FCSTD DOCUMENT  (FreeCAD 0.16R6712 (Git))
Label: LT arm cylinder geometry
License: All rights reserved
LicenseURL: http://en.wikipedia.org/wiki/All_rights_reserved
objects: Sketcher::SketchObject×5
note: 5 computed .brp shape members not serialized (recipe doc carries the construction recipe); baked Part::Feature solids carry a one-line shape summary decoded from their .brp

FEATURE [Sketcher::SketchObject] Sketch  label="16" stroke"
  Placement = pos=(0,0,0) rot=(-1,0,0;4.71239rad)
  sketch-geometry (6):
    g0: LineSegment [constr] StartX=0 StartY=0 StartZ=0 EndX=534.236 EndY=398.933 EndZ=0
    g1: LineSegment [constr] StartX=0 StartY=0 StartZ=0 EndX=0 EndY=557.181 EndZ=0
    g2: LineSegment [constr] StartX=0 StartY=557.181 StartZ=0 EndX=534.236 EndY=398.933 EndZ=0
    g3: LineSegment [constr] StartX=0 StartY=0 StartZ=0 EndX=179.648 EndY=642.092 EndZ=0
    g4: LineSegment [constr] StartX=179.648 StartY=642.092 StartZ=0 EndX=289.148 EndY=1033.46 EndZ=0
    g5: LineSegment [constr] StartX=0 StartY=557.181 StartZ=0 EndX=289.148 EndY=1033.46 EndZ=0
  constraints (16):
    c: Coincident(g0,g-1)
    c: Coincident(g1,g-1)
    c: Vertical(g1)
    c: Coincident(g2,g1)
    c: Coincident(g2,g0)
    c: Coincident(g3,g-1)
    c: Coincident(g4,g3)
    c: Parallel(g4,g3)
    c: Equal(g3,g0)
    c: Coincident(g5,g1)
    c: Coincident(g5,g4)
    c: Equal(g2,g5)
    c: Equal(g2,g1)
    c: Distance(g0) = 666.75
    c: Distance(g4) = 406.4
    c: Angle(g1,g2) = 1.28282
FEATURE [Sketcher::SketchObject] Sketch001  label="24" stroke"
  Placement = pos=(0,0,0) rot=(-1,0,0;4.71239rad)
  sketch-geometry (6):
    g0: LineSegment [constr] StartX=0 StartY=0 StartZ=0 EndX=712.621 EndY=498.983 EndZ=0
    g1: LineSegment [constr] StartX=0 StartY=0 StartZ=0 EndX=0 EndY=758.356 EndZ=0
    g2: LineSegment [constr] StartX=0 StartY=758.356 StartZ=0 EndX=712.621 EndY=498.983 EndZ=0
    g3: LineSegment [constr] StartX=0 StartY=0 StartZ=0 EndX=191.394 EndY=848.635 EndZ=0
    g4: LineSegment [constr] StartX=191.394 StartY=848.635 StartZ=0 EndX=325.509 EndY=1443.3 EndZ=0
    g5: LineSegment [constr] StartX=0 StartY=758.356 StartZ=0 EndX=325.509 EndY=1443.3 EndZ=0
  constraints (16):
    c: Coincident(g0,g-1)
    c: Coincident(g1,g-1)
    c: Vertical(g1)
    c: Coincident(g2,g1)
    c: Coincident(g2,g0)
    c: Coincident(g3,g-1)
    c: Coincident(g4,g3)
    c: Parallel(g4,g3)
    c: Equal(g3,g0)
    c: Coincident(g5,g1)
    c: Coincident(g5,g4)
    c: Equal(g2,g5)
    c: Distance(g0) = 869.95
    c: Equal(g2,g1)
    c: Distance(g4) = 609.6
    c: Angle(g1,g2) = 1.22173
FEATURE [Sketcher::SketchObject] Sketch002  label="30" stroke"
  Placement = pos=(0,0,0) rot=(-1,0,0;4.71239rad)
  sketch-geometry (6):
    g0: LineSegment [constr] StartX=0 StartY=0 StartZ=0 EndX=847.68 EndY=571.522 EndZ=0
    g1: LineSegment [constr] StartX=0 StartY=0 StartZ=0 EndX=0 EndY=914.4 EndZ=0
    g2: LineSegment [constr] StartX=0 StartY=914.4 StartZ=0 EndX=847.68 EndY=571.522 EndZ=0
    g3: LineSegment [constr] StartX=0 StartY=0 StartZ=0 EndX=224.033 EndY=997.501 EndZ=0
    g4: LineSegment [constr] StartX=224.033 StartY=997.501 StartZ=0 EndX=391.014 EndY=1740.98 EndZ=0
    g5: LineSegment [constr] StartX=0 StartY=914.4 StartZ=0 EndX=391.014 EndY=1740.98 EndZ=0
  constraints (16):
    c: Coincident(g0,g-1)
    c: Coincident(g1,g-1)
    c: Vertical(g1)
    c: Coincident(g2,g1)
    c: Coincident(g2,g0)
    c: Coincident(g3,g-1)
    c: Coincident(g4,g3)
    c: Parallel(g4,g3)
    c: Equal(g3,g0)
    c: Coincident(g5,g1)
    c: Coincident(g5,g4)
    c: Equal(g2,g5)
    c: Distance(g0) = 1022.35
    c: Equal(g2,g1)
    c: Distance(g4) = 762
    c: Distance(g1) = 914.4
FEATURE [Sketcher::SketchObject] Sketch003  label="36" stroke"
  Placement = pos=(0,0,0) rot=(-1,0,0;4.71239rad)
  sketch-geometry (6):
    g0: LineSegment [constr] StartX=0 StartY=0 StartZ=0 EndX=985.626 EndY=639.202 EndZ=0
    g1: LineSegment [constr] StartX=0 StartY=0 StartZ=0 EndX=0 EndY=1079.5 EndZ=0
    g2: LineSegment [constr] StartX=0 StartY=1079.5 StartZ=0 EndX=985.626 EndY=639.202 EndZ=0
    g3: LineSegment [constr] StartX=0 StartY=0 StartZ=0 EndX=296.398 EndY=1136.74 EndZ=0
    g4: LineSegment [constr] StartX=296.398 StartY=1136.74 StartZ=0 EndX=527.109 EndY=2021.56 EndZ=0
    g5: LineSegment [constr] StartX=0 StartY=1079.5 StartZ=0 EndX=527.109 EndY=2021.56 EndZ=0
  constraints (16):
    c: Coincident(g0,g-1)
    c: Coincident(g1,g-1)
    c: Vertical(g1)
    c: Coincident(g2,g1)
    c: Coincident(g2,g0)
    c: Coincident(g3,g-1)
    c: Coincident(g4,g3)
    c: Parallel(g4,g3)
    c: Equal(g3,g0)
    c: Coincident(g5,g1)
    c: Coincident(g5,g4)
    c: Equal(g2,g5)
    c: Distance(g0) = 1174.75
    c: Equal(g2,g1)
    c: Distance(g4) = 914.4
    c: Distance(g1) = 1079.5
FEATURE [Sketcher::SketchObject] Sketch004  label="Curl cylinder 14" stroke"
  sketch-geometry (6):
    g0: LineSegment [constr] StartX=212.811 StartY=105.674 StartZ=0 EndX=0 EndY=0 EndZ=0
    g1: LineSegment [constr] StartX=0 StartY=0 StartZ=0 EndX=-752.975 EndY=0 EndZ=0
    g2: LineSegment [constr] StartX=0 StartY=0 StartZ=0 EndX=-162.045 EndY=173.772 EndZ=0
    g3: LineSegment [constr] StartX=-752.975 StartY=0 StartZ=0 EndX=-162.045 EndY=173.772 EndZ=0
    g4: LineSegment [constr] StartX=-752.975 StartY=0 StartZ=0 EndX=-140.679 EndY=66.9959 EndZ=0
    g5: LineSegment [constr] StartX=-140.679 StartY=66.9959 StartZ=0 EndX=212.811 EndY=105.674 EndZ=0
  constraints (17):
    c: PointOnObject(g0,g-1)
    c: PointOnObject(g0,g-2)
    c: Coincident(g1,g-1)
    c: Horizontal(g1)
    c: Coincident(g2,g-1)
    c: Coincident(g3,g1)
    c: Coincident(g3,g2)
    c: Equal(g2,g0)
    c: Distance(g3) = 615.95
    c: Equal(g3,g4) = 666.75
    c: Coincident(g4,g1)
    c: Coincident(g4,g5)
    c: Parallel(g5,g4)
    c: Distance(g5) = 355.6
    c: Coincident(g5,g0)
    c: Distance(g0) = 237.604
    c: Angle(g2,g1) = 0.820305
